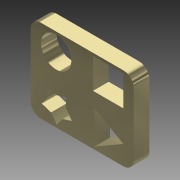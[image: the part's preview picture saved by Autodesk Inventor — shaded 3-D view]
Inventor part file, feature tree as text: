
AUTODESK INVENTOR PART (.ipt)
format: ipt  version: 2015 (Build 190159000, 159)  size: 153,088 bytes
history: native  units: in
note: dims shown in document units (in); Inventor stores cm internally (conversion verified against a paired STEP export)
features: extrude x1, shell x1, sketch x1
ambient origin geometry x8: Origin, YZ Plane, XZ Plane, XY Plane, X Axis, Y Axis, Z Axis, Center Point
bodies: Body1 (feature_tree)
feature tree (3):
  extrude  "Extrusion2"  Depth=0.2in
  shell  "Shell4"  Thickness=0.58in
  sketch  "Sketch1"  dims[d1=1.59in d2=0.2in d3=0.58in d4=0.49in d5=0.34in d6=0.58in d7=0.58in d8=0.05in d9=0.2in d18=0.638in d38=0.3in d39=0.0in d40=0.01in]
